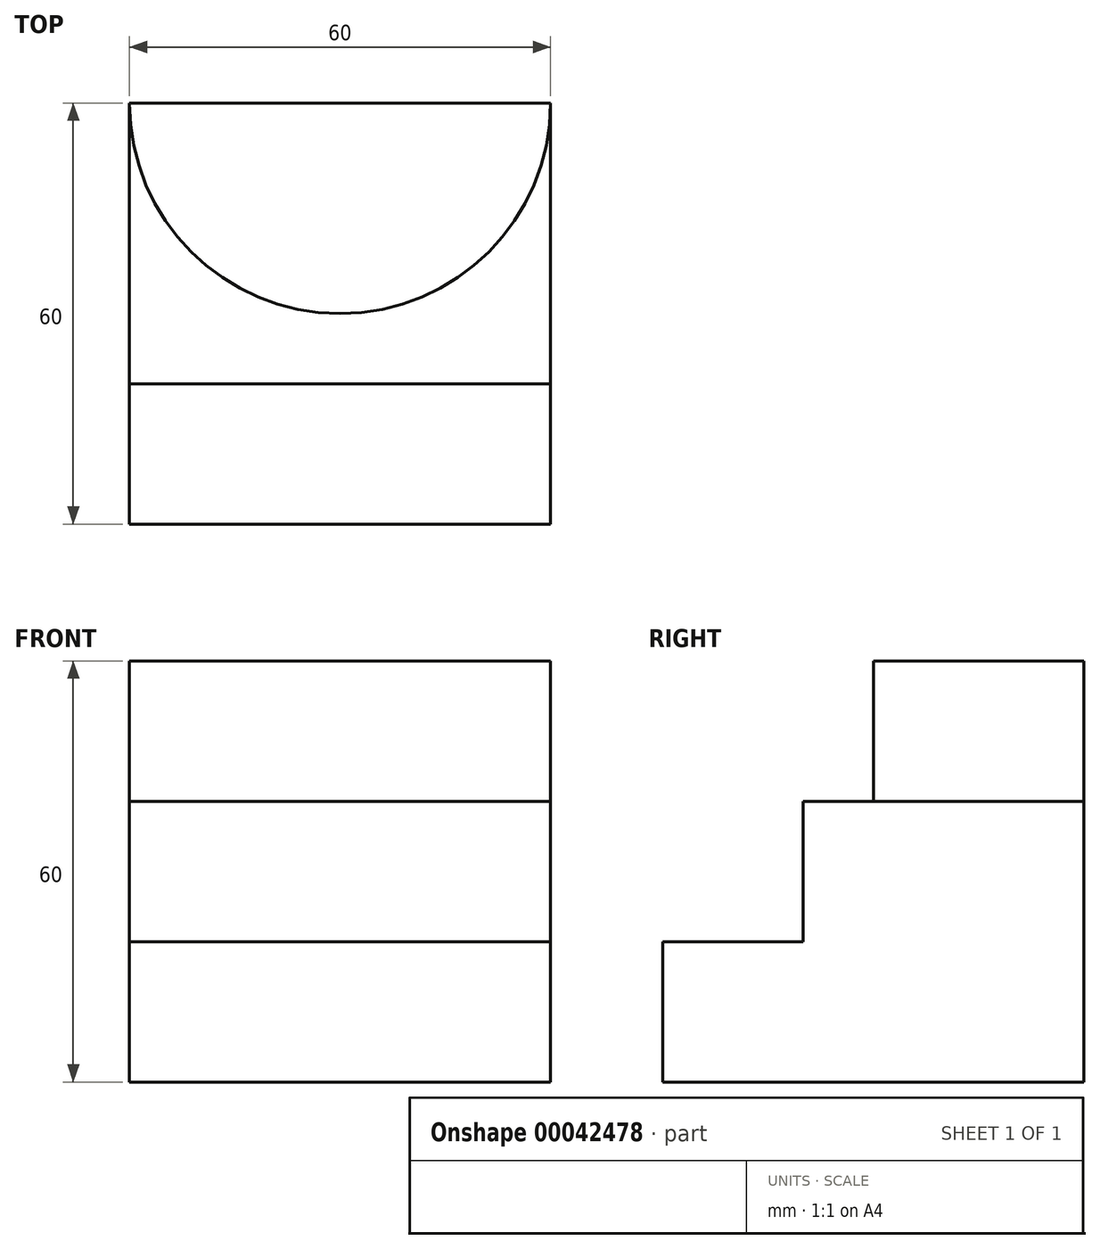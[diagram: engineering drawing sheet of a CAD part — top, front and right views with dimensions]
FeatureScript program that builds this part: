
annotation { "Feature Type Name" : "Feature", "Feature Type Description" : "" }
export const myFeature = defineFeature(function(context is Context, id is Id, definition is map)
    precondition{}
    {
        {
            var Q0;
            Q0=qCreatedBy(makeId("Top.planeOp"),FACE);
            var sketch = newSketch(context, id + "F0", { "sketchPlane" : qUnion([Q0])});
            skLineSegment(sketch, "E0.bottom", {"start": v(0, 0) * mm, "end": v(60, 0) * mm});
            skLineSegment(sketch, "E0.top", {"start": v(0, -60) * mm, "end": v(60, -60) * mm});
            skLineSegment(sketch, "E0.left", {"start": v(0, 0) * mm, "end": v(0, -60) * mm});
            skLineSegment(sketch, "E0.right", {"start": v(60, 0) * mm, "end": v(60, -60) * mm});
            skLineSegment(sketch, "E1", {"start": v(0, -40) * mm, "end": v(60, -40) * mm});
            skArc(sketch, "E2", {"start": v(0, 0) * mm, "mid": v(30, -30) * mm, "end": v(60, 0) * mm});
            skSolve(sketch);
        }
        {
            var Q0;
            Q0=makeQuery(id+"F0.imprint","IMPRINT",FACE,{"disambiguationData":[TD([[makeQuery(id+"F0.imprint","IMPRINT",EDGE,{"derivedFrom":sQuery(id+"F0.wireOp",EDGE,"E0.bottom")}),-1.0]])]});
            extrude(context, id + "F1", {"entities" : qUnion([Q0]), "depth" : 60 * mm});
        }
        {
            var Q0;
            {var subQ1=sQuery(id+"F0.wireOp",EDGE,"E1");Q0=makeQuery(id+"F0.imprint","IMPRINT",FACE,{"disambiguationData":[TD([[makeQuery(id+"F0.imprint","IMPRINT",EDGE,{"derivedFrom":subQ1}),1.0]])]});}
            extrude(context, id + "F2", {"entities" : qUnion([Q0]), "operationType" : NewBodyOperationType.ADD, "depth" : 40 * mm});
        }
        {
            var Q0;
            {var subQ2=sQuery(id+"F0.wireOp",EDGE,"E0.top");Q0=makeQuery(id+"F0.imprint","IMPRINT",FACE,{"disambiguationData":[TD([[makeQuery(id+"F0.imprint","IMPRINT",EDGE,{"derivedFrom":subQ2}),1.0]])]});}
            extrude(context, id + "F3", {"entities" : qUnion([Q0]), "operationType" : NewBodyOperationType.ADD, "depth" : 20 * mm});
        }
    });
